# Revit family: Haworth_BeHold_Modular_CredenzaForHAT
name_source: partatom
category: Furniture Systems
revit_build: Autodesk Revit 2018 (Build: 20170223_1515(x64)
units: mm (PartAtom-declared; Revit-internal decimal feet)

## family parameters
Always vertical = Yes
Cut with Voids When Loaded = No
OmniClass Number = 23.40.70.14.64.21
OmniClass Title = Systems Furniture
Part Type = Normal
Room Calculation Point = No
Round Connector Dimension = Use Diameter
Shared = No
Work Plane-Based = No

## types (5) — shared parameters
Actual Height = 22"
Assembly Code = E2020200
Back Door Height = 20 3/16"
Bag Liner Finish = Haworth _ Paint _ Sky Blue
Bag Liner Width = 36"
Blade Pull = Yes
Bottom Case Offset = 1/2"
Bottom Drawer Height = 13 149/256"
Bottom Drawer Offset = 1 3/8"
Case Thickness = 3/4"
Classic Pull = No
Classic Pull Length = 6 3/4"
Cresent Pull = No
Custom Size = No
Cutout = Yes
Description = Haworth - Be_Hold - Credenza For HAT
Distance Between Drawer = 1/8"
Front Door Height = 20 3/8"
Glide Finish = Haworth _ Polymer _ Slate
Linear Pull = No
Linear Pull Length = 8"
Manufacturer = Haworth
Max. Depth = 24"
Max. Height = 22"
Min. Height = 22"
Min. Storage Width = 30"
Min. Width = 60"
Model = Haworth Be_Hold
Revision Number = 1
Separator Offset = 9 3/16"
Shelf 1 Offset = 13 5/16"
Shelf Finish = Haworth _ Paint _ Sky Blue
Size = Verify Final Dim. w/ Haworth
Steel Shelf Width = 36"
Sustainability Info = https://www.haworth.com
Top Drawer Height = 6 203/256"
Top Thickness = 3/4"
Total Drawer Height = 20 1/2"
Trim Finish = Haworth _ Paint _ Smooth Plaster
URL = www.haworth.com
URL - Product = http://www.haworth.com
Void Back Offset = 3 15/16"
Void Dimension = 4"
Warranty = http://www.haworth.com
Wing Pull = No
Wing Pull Length = 16 3/4"
With Lock = Yes

## per-type parameters (varying)
- 24d 78w - 42w Drawer - Inset Back: Actual Bag Liner=No; Actual Depth=24"; Actual Steel Shelf=No; Actual Storage Width=42"; Actual Width=78"; Back Case Back Control=3/16"; Back Case Side Control=3/4"; Bag Liner=No; Bag Liner Side Offset=25/64"; Blade Pull Length=41 13/16"; Cutout Dimension=2"; Depth=24"; Door Width=37 1/2"; Drawer Width=41 7/8"; Drawers=Yes; HAT Shelf Control=Yes; Inset Style=Yes; Max. Storage Width=42"; Max. Width=78"; Mid Separator O/D Control=Yes; Mid Separator S/D Control=No; Min. Depth=16"; Open=No; Proud Style=No; Separator Case Front Offset=3/4"; Shelf=No; Shelf Front Offset=3/4"; Side Case Back Control=0"; Side Case Front Control=3/4"; Sliding Door=No; Standard Depths=16, 24 in.; Standard Widths=60-78 @ 6in. increments; Storage Shelf Control=No; Storage Width=42"; Top Case Back Control=3/16"; Top Case Front Offset=3"; Width=78"
- 24d 72w - 36w Door - Inset Back: Actual Bag Liner=No; Actual Depth=24"; Actual Steel Shelf=No; Actual Storage Width=36"; Actual Width=72"; Back Case Back Control=3/16"; Back Case Side Control=3/4"; Bag Liner=No; Bag Liner Side Offset=39/64"; Blade Pull Length=35 13/16"; Cutout Dimension=2"; Depth=24"; Door Width=34 1/2"; Drawer Width=35 7/8"; Drawers=No; HAT Shelf Control=Yes; Inset Style=Yes; Max. Storage Width=36"; Max. Width=72"; Mid Separator O/D Control=No; Mid Separator S/D Control=Yes; Min. Depth=24"; Open=No; Proud Style=No; Separator Case Front Offset=3/4"; Shelf=No; Shelf Front Offset=2 1/8"; Side Case Back Control=0"; Side Case Front Control=0"; Sliding Door=Yes; Standard Depths=24 in.; Standard Widths=60-72 @ 6 in. increments; Storage Shelf Control=Yes; Storage Width=36"; Top Case Back Control=3/16"; Top Case Front Offset=2 1/2"; Width=72"
- 24d 72w - 36w Open - Inset Back: Actual Bag Liner=No; Actual Depth=24"; Actual Steel Shelf=No; Actual Storage Width=36"; Actual Width=72"; Back Case Back Control=3/16"; Back Case Side Control=3/4"; Bag Liner=No; Bag Liner Side Offset=25/64"; Blade Pull Length=35 13/16"; Cutout Dimension=2"; Depth=24"; Door Width=34 1/2"; Drawer Width=35 7/8"; Drawers=No; HAT Shelf Control=Yes; Inset Style=Yes; Max. Storage Width=36"; Max. Width=72"; Mid Separator O/D Control=Yes; Mid Separator S/D Control=No; Min. Depth=16"; Open=Yes; Proud Style=No; Separator Case Front Offset=0"; Shelf=No; Shelf Front Offset=3/4"; Side Case Back Control=0"; Side Case Front Control=0"; Sliding Door=No; Standard Depths=16, 24 in.; Standard Widths=60-72 @ 6 in. increments; Storage Shelf Control=Yes; Storage Width=36"; Top Case Back Control=3/16"; Top Case Front Offset=3"; Width=72"
- 16d 72w - 36w Open - Proud Back: Actual Bag Liner=Yes; Actual Depth=16"; Actual Steel Shelf=Yes; Actual Storage Width=36"; Actual Width=72"; Back Case Back Control=0"; Back Case Side Control=0"; Bag Liner=Yes; Bag Liner Side Offset=25/64"; Blade Pull Length=35 13/16"; Cutout Dimension=1/2"; Depth=16"; Door Width=34 1/2"; Drawer Width=35 7/8"; Drawers=No; HAT Shelf Control=No; Inset Style=No; Max. Storage Width=36"; Max. Width=72"; Mid Separator O/D Control=Yes; Mid Separator S/D Control=No; Min. Depth=16"; Open=Yes; Proud Style=Yes; Separator Case Front Offset=0"; Shelf=Yes; Shelf Front Offset=3/4"; Side Case Back Control=3/4"; Side Case Front Control=0"; Sliding Door=No; Standard Depths=16, 24 in.; Standard Widths=60-72 @ 6 in. increments; Storage Shelf Control=Yes; Storage Width=36"; Top Case Back Control=0"; Top Case Front Offset=3"; Width=72"
- 16d 78w - 42w Drawers - Proud Back: Actual Bag Liner=Yes; Actual Depth=16"; Actual Steel Shelf=Yes; Actual Storage Width=42"; Actual Width=78"; Back Case Back Control=0"; Back Case Side Control=0"; Bag Liner=Yes; Bag Liner Side Offset=25/64"; Blade Pull Length=41 13/16"; Cutout Dimension=1/2"; Depth=16"; Door Width=37 1/2"; Drawer Width=41 7/8"; Drawers=Yes; HAT Shelf Control=No; Inset Style=No; Max. Storage Width=42"; Max. Width=78"; Mid Separator O/D Control=Yes; Mid Separator S/D Control=No; Min. Depth=16"; Open=No; Proud Style=Yes; Separator Case Front Offset=3/4"; Shelf=Yes; Shelf Front Offset=3/4"; Side Case Back Control=3/4"; Side Case Front Control=3/4"; Sliding Door=No; Standard Depths=16, 24 in.; Standard Widths=60-78 @ 6in. increments; Storage Shelf Control=No; Storage Width=42"; Top Case Back Control=0"; Top Case Front Offset=3"; Width=78"

## geometry (parser evidence)
native form markers: Sweep x12
no freeform markers — native parametric forms only
